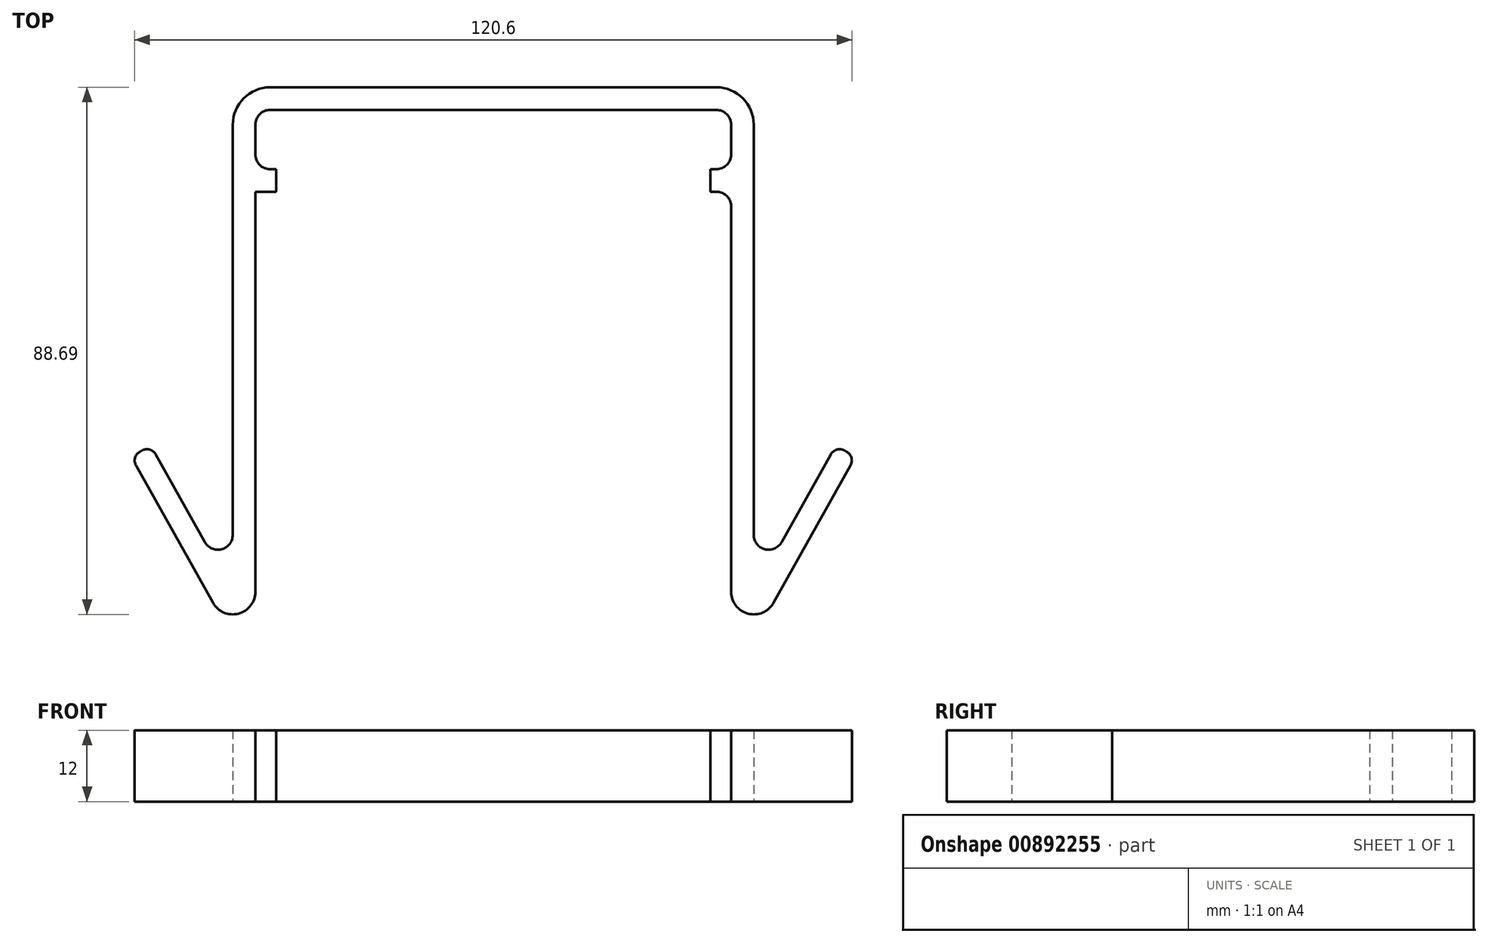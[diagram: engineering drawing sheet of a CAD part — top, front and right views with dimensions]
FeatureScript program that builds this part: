
annotation { "Feature Type Name" : "Feature", "Feature Type Description" : "" }
export const myFeature = defineFeature(function(context is Context, id is Id, definition is map)
    precondition{}
    {
        {
            var Q0;
            Q0=qCreatedBy(makeId("Top.planeOp"),FACE);
            var sketch = newSketch(context, id + "F0", { "sketchPlane" : qUnion([Q0])});
            skLineSegment(sketch, "E0", {"start": v(-37.5, 43.98) * mm, "end": v(0, 43.98) * mm});
            skPoint(sketch, "E1.visualSharp", {"position": v(40, 43.98) * mm});
            skArc(sketch, "E1.filletArc", {"start": v(40, 41.48) * mm, "mid": v(39.27, 43.24) * mm, "end": v(37.5, 43.98) * mm});
            skPoint(sketch, "E2.visualSharp", {"position": v(-40, 43.98) * mm});
            skArc(sketch, "E2.filletArc", {"start": v(-37.5, 43.98) * mm, "mid": v(-39.27, 43.24) * mm, "end": v(-40, 41.48) * mm});
            skArc(sketch, "E3.filletArc", {"start": v(-40, 36.48) * mm, "mid": v(-39.27, 34.7) * mm, "end": v(-37.5, 33.98) * mm});
            skLineSegment(sketch, "E4", {"start": v(-37.5, 47.78) * mm, "end": v(0, 47.78) * mm});
            skLineSegment(sketch, "E5", {"start": v(43.81, 41.47) * mm, "end": v(43.81, -27.53) * mm});
            skLineSegment(sketch, "E6", {"start": v(-43.81, 41.47) * mm, "end": v(-43.81, 36.48) * mm});
            skPoint(sketch, "E7.visualSharp", {"position": v(43.81, 47.78) * mm});
            skArc(sketch, "E7.filletArc", {"start": v(43.8, 41.47) * mm, "mid": v(41.96, 45.93) * mm, "end": v(37.5, 47.78) * mm});
            skPoint(sketch, "E8.visualSharp", {"position": v(-43.81, 47.78) * mm});
            skArc(sketch, "E8.filletArc", {"start": v(-37.5, 47.78) * mm, "mid": v(-41.96, 45.93) * mm, "end": v(-43.8, 41.47) * mm});
            skLineSegment(sketch, "E9", {"start": v(-37.5, 33.98) * mm, "end": v(-36.5, 33.98) * mm});
            skLineSegment(sketch, "E10", {"start": v(-37.5, 30.17) * mm, "end": v(-36.5, 30.17) * mm});
            skLineSegment(sketch, "E11", {"start": v(-36.5, 30.17) * mm, "end": v(-36.5, 33.98) * mm});
            skLineSegment(sketch, "E12", {"start": v(48.5, -28.75) * mm, "end": v(56.37, -14.7) * mm});
            skLineSegment(sketch, "E13", {"start": v(59.07, -13.34) * mm, "end": v(59.25, -13.44) * mm});
            skLineSegment(sketch, "E14", {"start": v(60.08, -15.86) * mm, "end": v(59.7, -16.55) * mm});
            skLineSegment(sketch, "E15", {"start": v(40, -37.1) * mm, "end": v(40, -37.1) * mm});
            skPoint(sketch, "E16.visualSharp", {"position": v(43.81, -37.1) * mm});
            skArc(sketch, "E16.filletArc", {"start": v(43.81, -27.53) * mm, "mid": v(45.68, -29.95) * mm, "end": v(48.5, -28.75) * mm});
            skPoint(sketch, "E17.visualSharp", {"position": v(40, -51.7) * mm});
            skArc(sketch, "E17.filletArc", {"start": v(40, -37.1) * mm, "mid": v(42.85, -40.8) * mm, "end": v(47.13, -38.97) * mm});
            skLineSegment(sketch, "E18", {"start": v(59.25, -13.44) * mm, "end": v(59.43, -13.54) * mm});
            skLineSegment(sketch, "E19", {"start": v(56.37, -14.7) * mm, "end": v(56.76, -14) * mm});
            skLineSegment(sketch, "E20", {"start": v(59.7, -16.55) * mm, "end": v(47.13, -38.97) * mm});
            skPoint(sketch, "E21.visualSharp", {"position": v(57.6, -12.51) * mm});
            skArc(sketch, "E21.filletArc", {"start": v(59.07, -13.34) * mm, "mid": v(57.78, -13.2) * mm, "end": v(56.76, -14) * mm});
            skPoint(sketch, "E22.visualSharp", {"position": v(60.91, -14.38) * mm});
            skArc(sketch, "E22.filletArc", {"start": v(60.08, -15.86) * mm, "mid": v(60.24, -14.57) * mm, "end": v(59.43, -13.54) * mm});
            skLineSegment(sketch, "E23", {"start": v(0, 47.78) * mm, "end": v(37.5, 47.78) * mm});
            skLineSegment(sketch, "E24", {"start": v(0, 43.98) * mm, "end": v(37.5, 43.98) * mm});
            skLineSegment(sketch, "E25.MirrorCS", {"start": v(-59.25, -13.44) * mm, "end": v(-59.43, -13.54) * mm});
            skLineSegment(sketch, "E26.MirrorCS", {"start": v(-59.07, -13.34) * mm, "end": v(-59.25, -13.44) * mm});
            skLineSegment(sketch, "E27.MirrorCS", {"start": v(36.5, 30.17) * mm, "end": v(36.5, 33.98) * mm});
            skArc(sketch, "E28.MirrorCS", {"start": v(-60.08, -15.86) * mm, "mid": v(-60.24, -14.57) * mm, "end": v(-59.43, -13.54) * mm});
            skArc(sketch, "E29.MirrorCS", {"start": v(-59.07, -13.34) * mm, "mid": v(-57.78, -13.2) * mm, "end": v(-56.76, -14) * mm});
            skArc(sketch, "E30.MirrorCS", {"start": v(37.5, 43.98) * mm, "mid": v(39.27, 43.24) * mm, "end": v(40, 41.48) * mm});
            skLineSegment(sketch, "E31.MirrorCS", {"start": v(-60.08, -15.86) * mm, "end": v(-59.7, -16.55) * mm});
            skLineSegment(sketch, "E32.MirrorCS", {"start": v(-56.37, -14.7) * mm, "end": v(-56.76, -14) * mm});
            skArc(sketch, "E33.MirrorCS", {"start": v(-40, 41.48) * mm, "mid": v(-39.27, 43.24) * mm, "end": v(-37.5, 43.98) * mm});
            skArc(sketch, "E34.MirrorCS", {"start": v(40, 36.48) * mm, "mid": v(39.27, 34.7) * mm, "end": v(37.5, 33.98) * mm});
            skLineSegment(sketch, "E35.MirrorCS", {"start": v(40, 41.48) * mm, "end": v(40, 36.48) * mm});
            skLineSegment(sketch, "E36.MirrorCS", {"start": v(0, 43.98) * mm, "end": v(-37.5, 43.98) * mm});
            skLineSegment(sketch, "E37.MirrorCS", {"start": v(37.5, 33.98) * mm, "end": v(36.5, 33.98) * mm});
            skLineSegment(sketch, "E38.MirrorCS", {"start": v(37.5, 43.98) * mm, "end": v(0, 43.98) * mm});
            skPoint(sketch, "E39.MirrorP", {"position": v(-57.6, -12.51) * mm});
            skLineSegment(sketch, "E40.MirrorCS", {"start": v(43.81, 41.47) * mm, "end": v(43.81, 36.48) * mm});
            skLineSegment(sketch, "E41.MirrorCS", {"start": v(-48.5, -28.75) * mm, "end": v(-56.37, -14.7) * mm});
            skLineSegment(sketch, "E42.MirrorCS", {"start": v(0, 47.78) * mm, "end": v(-37.5, 47.78) * mm});
            skPoint(sketch, "E43.MirrorP", {"position": v(-43.81, -37.1) * mm});
            skPoint(sketch, "E44.MirrorP", {"position": v(40, 36.4) * mm});
            skLineSegment(sketch, "E45.MirrorCS", {"start": v(37.5, 47.78) * mm, "end": v(0, 47.78) * mm});
            skArc(sketch, "E46.MirrorCS", {"start": v(-43.81, -27.53) * mm, "mid": v(-45.68, -29.95) * mm, "end": v(-48.5, -28.75) * mm});
            skPoint(sketch, "E47.MirrorP", {"position": v(-40, -51.7) * mm});
            skLineSegment(sketch, "E48.MirrorCS", {"start": v(-59.7, -16.55) * mm, "end": v(-47.13, -38.97) * mm});
            skLineSegment(sketch, "E49.MirrorCS", {"start": v(-40, -37.1) * mm, "end": v(-40, -37.1) * mm});
            skPoint(sketch, "E50.MirrorP", {"position": v(-60.91, -14.38) * mm});
            skLineSegment(sketch, "E51.MirrorCS", {"start": v(-43.81, 41.47) * mm, "end": v(-43.81, -27.53) * mm});
            skArc(sketch, "E52.MirrorCS", {"start": v(37.5, 47.78) * mm, "mid": v(41.96, 45.93) * mm, "end": v(43.8, 41.47) * mm});
            skArc(sketch, "E53.MirrorCS", {"start": v(-40, -37.1) * mm, "mid": v(-42.85, -40.8) * mm, "end": v(-47.13, -38.97) * mm});
            skLineSegment(sketch, "E54.MirrorCS", {"start": v(37.5, 30.17) * mm, "end": v(36.5, 30.17) * mm});
            skArc(sketch, "E55.MirrorCS", {"start": v(-43.8, 41.47) * mm, "mid": v(-41.96, 45.93) * mm, "end": v(-37.5, 47.78) * mm});
            skLineSegment(sketch, "E56.MirrorCS", {"start": v(-40, 41.48) * mm, "end": v(-40, 36.48) * mm});
            skLineSegment(sketch, "E57", {"start": v(-40, 30.17) * mm, "end": v(-40, -37.1) * mm});
            skPoint(sketch, "E58", {"position": v(-40, 30.17) * mm});
            skLineSegment(sketch, "E59", {"start": v(40, 27.82) * mm, "end": v(40, -37.1) * mm});
            skLineSegment(sketch, "E60", {"start": v(-40, 30.17) * mm, "end": v(-37.5, 30.17) * mm});
            skLineSegment(sketch, "E61", {"start": v(37.5, 30.17) * mm, "end": v(37.65, 30.17) * mm});
            skPoint(sketch, "E62.visualSharp", {"position": v(40, 30.16) * mm});
            skArc(sketch, "E62.filletArc", {"start": v(40, 27.82) * mm, "mid": v(39.31, 29.48) * mm, "end": v(37.65, 30.17) * mm});
            skSolve(sketch);
        }
        {
            var Q0;
            Q0=makeQuery(id+"F0.imprint","IMPRINT",FACE,{"disambiguationData":[TD([[makeQuery(id+"F0.imprint","IMPRINT",EDGE,{"derivedFrom":sQuery(id+"F0.wireOp",EDGE,"E3.filletArc")}),-1.0]])]});
            extrude(context, id + "F1", {"entities" : qUnion([Q0]), "depth" : 12 * mm, "offsetDistance" : 25 * mm});
        }
    });
